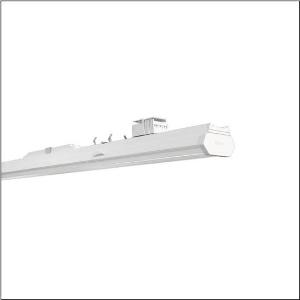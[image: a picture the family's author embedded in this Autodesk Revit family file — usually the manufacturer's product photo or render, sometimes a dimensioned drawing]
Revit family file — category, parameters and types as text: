
# Revit family: licross_r__11_protected_ho_51td12mn4f5m_c228
name_source: partatom
category: Lighting Fixtures
units: mm (PartAtom-declared; Revit-internal decimal feet)

## family parameters
Cut with Voids When Loaded = No
Host = Face
Light Source = No
Part Type = Normal
Room Calculation Point = No
Round Connector Dimension = Use Diameter
Shared = No

## types (1)
- --- (1 x LED, 15820 lm, 87.4 W, 4000K)
    Apparent Load = 87 VA
    CIE Flux Codes = 70 91 97 98 100
    Color Rendering = 80
    Color Temperature = 4000K
    Default Elevation = 1800 mm
    Description = Licross® 11 Protected HO, luminaire insert, of sheet steel, galvanised, coil coated, white, length: 1.500mm, width: 90mm, height: 101mm, LED rated luminous flux: 15.820lm, light colour: 840, control gear: ON/OFF Multilumen, with plug, 3-pole, with phase selection, mains connection: 220..240V, AC, 50/60Hz, rated input power: 87W, halogen-free wiring, primary light control with lens, of plastic, primary optical cover: cover, of PMMA, light emission: direct distribution, primary light characteristic: symmetric, protection rating (complete): IP54, insulation class (complete): insulation class I (protective earthing), certification: CE, ENEC, VDE, UKCA, protection symbol: D if used in an environment with non-conductive dust loads with corresponding accessories, impact resistance: IK06, permissible ambient temperature for indoor applications: -35..+35°C, corresponds to IFS (International Featured Standards) requirements for safety and quality in the food industry, reducing of maximum allowable ambient temperature of 5°C with ceiling mounting, LABS conformity tested according to VDMA 24364:2018-05, packaging unit: 1 piece
    Height = 92 mm
    Lamp = 1 x LED
    Lamp Light Flux = 15820 lm
    Lamp Power = 87.4 W
    Lamp count = 1
    Length = 1500 mm
    Luminous efficacy = 181 lm/W
    Manufacturer = Siteco
    ModVariant = No
    Model = 51TD12MN4F5M
    Mounting Place = Ceiling
    Mounting Type = Pendant
    Number of Poles = 1
    OnlyDefault = Yes
    Power Factor = 1
    Product Name = Licross® 11 Protected HO
    Product group = luminaire insert
    ProductGroupID = 901
    Protection Class = Protection class I
    Protection Degree = IP 54
    RLX_Detail_Level = 1
    RLX_Emergency_Light_Flux = 0 lm
    RLX_Emergency_Type = 0
    RLX_Emergency_Type_DB = No
    RlxData = <blob elided: 22065 chars, md5=0f8345e0>
    Socket = socket
    Standby Power = 0 W
    System Light Flux = 15820 lm
    System Power = 87 W
    Type Comments = factory setting: luminous flux: 100 % | (A | C | E) | 203 mA
    Type Image = l_1256145.jpg
    URL = http://relux.com
    VarID = @adj_019511
    Voltage = 0 V
    Weight = 0.00 kg
    Width = 88 mm

## geometry (parser evidence)
native form markers: Blend x4, Sweep x11
no freeform markers — native parametric forms only
